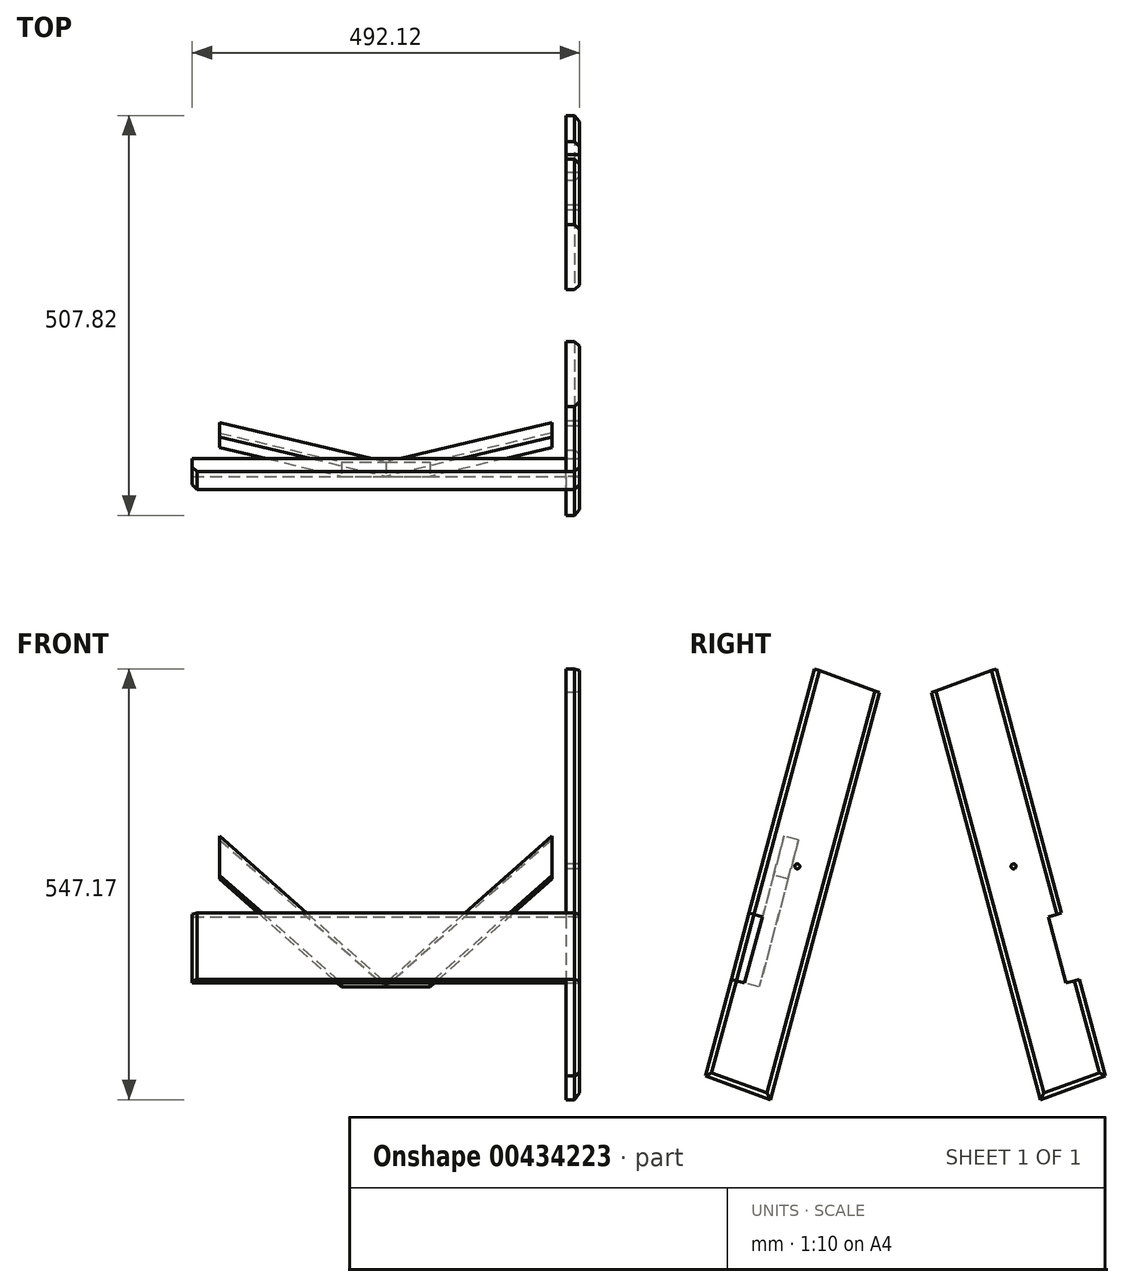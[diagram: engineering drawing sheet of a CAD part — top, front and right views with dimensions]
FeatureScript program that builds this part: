
annotation { "Feature Type Name" : "Feature", "Feature Type Description" : "" }
export const myFeature = defineFeature(function(context is Context, id is Id, definition is map)
    precondition{}
    {
        {
            var Q0;
            Q0=qCreatedBy(makeId("Right.planeOp"),FACE);
            var sketch = newSketch(context, id + "F0", { "sketchPlane" : qUnion([Q0])});
            skCircle(sketch, "E0", {"center": v(0, 0) * mm, "radius": 3.17 * mm, "construction": true});
            skCircle(sketch, "E1", {"center": v(0, 0) * mm, "radius": 43.66 * mm, "construction": true});
            skLineSegment(sketch, "E2", {"start": v(0, 0) * mm, "end": v(89.25, -32.49) * mm, "construction": true});
            skLineSegment(sketch, "E3", {"start": v(-42.17, 11.3) * mm, "end": v(42.17, -11.3) * mm, "construction": true});
            skLineSegment(sketch, "E4", {"start": v(22, 250.8) * mm, "end": v(-61.1, -59.39) * mm});
            skLineSegment(sketch, "E5", {"start": v(104.36, 220.82) * mm, "end": v(-34.22, -296.38) * mm});
            skLineSegment(sketch, "E6", {"start": v(22, 250.8) * mm, "end": v(104.36, 220.82) * mm});
            skLineSegment(sketch, "E7", {"start": v(-116.58, -266.4) * mm, "end": v(-34.22, -296.38) * mm});
            skCircle(sketch, "E8", {"center": v(0, 0) * mm, "radius": 3.13 * mm});
            skLineSegment(sketch, "E9", {"start": v(137.33, 282.03) * mm, "end": v(137.33, -341.7) * mm, "construction": true});
            skCircle(sketch, "E10.MirrorC", {"center": v(274.67, 0) * mm, "radius": 3.13 * mm});
            skCircle(sketch, "E11.MirrorC", {"center": v(274.67, 0) * mm, "radius": 3.17 * mm, "construction": true});
            skCircle(sketch, "E12.MirrorC", {"center": v(274.67, 0) * mm, "radius": 43.66 * mm, "construction": true});
            skLineSegment(sketch, "E13.MirrorCS", {"start": v(274.67, 0) * mm, "end": v(185.41, -32.49) * mm, "construction": true});
            skLineSegment(sketch, "E14.MirrorCS", {"start": v(316.83, 11.3) * mm, "end": v(232.5, -11.3) * mm, "construction": true});
            skLineSegment(sketch, "E15.MirrorCS", {"start": v(170.3, 220.82) * mm, "end": v(308.88, -296.38) * mm});
            skLineSegment(sketch, "E16.MirrorCS", {"start": v(252.66, 250.8) * mm, "end": v(170.3, 220.82) * mm});
            skLineSegment(sketch, "E17.MirrorCS", {"start": v(391.24, -266.4) * mm, "end": v(308.88, -296.38) * mm});
            skLineSegment(sketch, "E18", {"start": v(-61.1, -59.39) * mm, "end": v(-44.24, -63.9) * mm});
            skLineSegment(sketch, "E19", {"start": v(-44.24, -63.9) * mm, "end": v(-66.84, -148.25) * mm});
            skLineSegment(sketch, "E20", {"start": v(-66.84, -148.25) * mm, "end": v(-83.7, -143.73) * mm});
            skLineSegment(sketch, "E21.trimOffspring", {"start": v(-83.7, -143.73) * mm, "end": v(-116.58, -266.4) * mm});
            skLineSegment(sketch, "E22.MirrorCS", {"start": v(318.9, -63.9) * mm, "end": v(341.5, -148.25) * mm});
            skLineSegment(sketch, "E23.MirrorCS", {"start": v(335.77, -59.39) * mm, "end": v(318.9, -63.9) * mm});
            skLineSegment(sketch, "E24.MirrorCS", {"start": v(341.5, -148.25) * mm, "end": v(358.37, -143.73) * mm});
            skLineSegment(sketch, "E25.MirrorCS", {"start": v(252.66, 250.8) * mm, "end": v(335.77, -59.39) * mm});
            skLineSegment(sketch, "E26.MirrorCS", {"start": v(358.37, -143.73) * mm, "end": v(391.24, -266.4) * mm});
            skSolve(sketch);
        }
        {
            var Q0;
            Q0 = qSketchRegion(id + "F0", true);
            var Q1;
            Q1=makeQuery(id+"F0.imprint","IMPRINT",FACE,{"disambiguationData":[TD([[makeQuery(id+"F0.imprint","IMPRINT",EDGE,{"derivedFrom":sQuery(id+"F0.wireOp",EDGE,"E4")}),1.0]])]});
            extrude(context, id + "F1", {"entities" : qUnion([Q0, Q1]), "depth" : 17.46 * mm});
        }
        {
            var Q0;
            Q0=makeQuery(id+"F1.opExtrude","CAP_FACE",FACE,{"disambiguationData":[OSD([sQuery(id+"F0.wireOp",EDGE,"E4"),sQuery(id+"F0.wireOp",EDGE,"E5"),sQuery(id+"F0.wireOp",EDGE,"E6"),sQuery(id+"F0.wireOp",EDGE,"E7"),sQuery(id+"F0.wireOp",EDGE,"E8"),sQuery(id+"F0.wireOp",EDGE,"E18"),sQuery(id+"F0.wireOp",EDGE,"E19"),sQuery(id+"F0.wireOp",EDGE,"E20"),sQuery(id+"F0.wireOp",EDGE,"E21.trimOffspring")])],"isStart":false});
            var sketch = newSketch(context, id + "F2", { "sketchPlane" : qUnion([Q0])});
            skLineSegment(sketch, "E27", {"start": v(-44.24, -63.9) * mm, "end": v(-66.84, -148.25) * mm});
            skLineSegment(sketch, "E28", {"start": v(-66.84, -148.25) * mm, "end": v(-83.7, -143.73) * mm});
            skLineSegment(sketch, "E29", {"start": v(-83.7, -143.73) * mm, "end": v(-61.1, -59.39) * mm});
            skLineSegment(sketch, "E30", {"start": v(-61.1, -59.39) * mm, "end": v(-46.15, -63.4) * mm});
            skSolve(sketch);
        }
        {
            var Q0;
            Q0 = qSketchRegion(id + "F2", true);
            var Q1;
            {var subQ1=sQuery(id+"F2.wireOp",EDGE,"E27");Q1=makeQuery(id+"F2.imprint","IMPRINT",FACE,{"disambiguationData":[TD([[makeQuery(id+"F2.imprint","IMPRINT",EDGE,{"derivedFrom":subQ1}),-1.0]])]});}
            extrude(context, id + "F3", {"entities" : qUnion([Q0, Q1]), "depth" : -492.12 * mm});
        }
        {
            var Q0;
            Q0=makeQuery(id+"F3.opExtrude","CAP_EDGE",EDGE,{"disambiguationData":[OSD([sQuery(id+"F2.wireOp",EDGE,"E29")])],"isStart":true});
            var Q1;
            Q1=makeQuery(id+"F1.opExtrude","CAP_EDGE",EDGE,{"disambiguationData":[OSD([sQuery(id+"F0.wireOp",EDGE,"E4")])],"isStart":false});
            var Q2;
            Q2=makeQuery(id+"F1.opExtrude","CAP_EDGE",EDGE,{"disambiguationData":[OSD([sQuery(id+"F0.wireOp",EDGE,"E5")])],"isStart":false});
            var Q3;
            Q3=makeQuery(id+"F1.opExtrude","CAP_EDGE",EDGE,{"disambiguationData":[OSD([sQuery(id+"F0.wireOp",EDGE,"E21.trimOffspring")])],"isStart":false});
            var Q4;
            Q4=makeQuery(id+"F1.opExtrude","CAP_EDGE",EDGE,{"disambiguationData":[OSD([sQuery(id+"F0.wireOp",EDGE,"E7")])],"isStart":false});
            var Q5;
            Q5=makeQuery(id+"F1.opExtrude","CAP_EDGE",EDGE,{"disambiguationData":[OSD([sQuery(id+"F0.wireOp",EDGE,"E15.MirrorCS")])],"isStart":false});
            var Q6;
            Q6=makeQuery(id+"F1.opExtrude","CAP_EDGE",EDGE,{"disambiguationData":[OSD([sQuery(id+"F0.wireOp",EDGE,"E25.MirrorCS")])],"isStart":false});
            var Q7;
            Q7=makeQuery(id+"F1.opExtrude","CAP_EDGE",EDGE,{"disambiguationData":[OSD([sQuery(id+"F0.wireOp",EDGE,"E26.MirrorCS")])],"isStart":false});
            var Q8;
            Q8=makeQuery(id+"F1.opExtrude","CAP_EDGE",EDGE,{"disambiguationData":[OSD([sQuery(id+"F0.wireOp",EDGE,"E17.MirrorCS")])],"isStart":false});
            var Q9;
            Q9=makeQuery(id+"F3.opExtrude","CAP_EDGE",EDGE,{"disambiguationData":[OSD([sQuery(id+"F2.wireOp",EDGE,"E29")])],"isStart":false});
            chamfer(context, id + "F4", {"entities" : qUnion([Q0, Q1, Q2, Q3, Q4, Q5, Q6, Q7, Q8, Q9]), "width" : 6.35 * mm, "tangentPropagation" : true});
        }
        {
            var Q0;
            Q0=makeQuery(id+"F3.opExtrude","SWEPT_FACE",FACE,{"disambiguationData":[OSD([sQuery(id+"F2.wireOp",EDGE,"E27")])]});
            var sketch = newSketch(context, id + "F5", { "sketchPlane" : qUnion([Q0])});
            skLineSegment(sketch, "E31.MirrorCS", {"start": v(17.46, -18.7) * mm, "end": v(172.2, -160.5) * mm});
            skLineSegment(sketch, "E32.MirrorCS", {"start": v(172.2, -160.5) * mm, "end": v(228.6, -160.5) * mm});
            skLineSegment(sketch, "E33", {"start": v(17.46, -18.7) * mm, "end": v(17.46, -18.7) * mm});
            skLineSegment(sketch, "E34", {"start": v(17.46, 32.98) * mm, "end": v(228.6, -160.5) * mm});
            skLineSegment(sketch, "E35.bottom", {"start": v(17.46, 32.98) * mm, "end": v(439.74, 32.98) * mm, "construction": true});
            skLineSegment(sketch, "E35.right", {"start": v(439.74, 32.98) * mm, "end": v(439.74, -160.5) * mm, "construction": true});
            skLineSegment(sketch, "E36.bottom", {"start": v(439.74, 32.98) * mm, "end": v(474.66, 32.98) * mm, "construction": true});
            skLineSegment(sketch, "E36.top", {"start": v(439.74, -160.5) * mm, "end": v(474.66, -160.5) * mm, "construction": true});
            skLineSegment(sketch, "E36.right", {"start": v(474.66, 32.98) * mm, "end": v(474.66, -160.5) * mm, "construction": true});
            skLineSegment(sketch, "E37.bottom", {"start": v(17.46, 32.98) * mm, "end": v(-17.46, 32.98) * mm, "construction": true});
            skLineSegment(sketch, "E37.top", {"start": v(17.46, -160.5) * mm, "end": v(-17.46, -160.5) * mm, "construction": true});
            skLineSegment(sketch, "E37.right", {"start": v(-17.46, 32.98) * mm, "end": v(-17.46, -160.5) * mm, "construction": true});
            skLineSegment(sketch, "E38", {"start": v(17.46, -160.5) * mm, "end": v(172.2, -160.5) * mm, "construction": true});
            skLineSegment(sketch, "E39", {"start": v(228.6, 32.98) * mm, "end": v(228.6, -160.5) * mm, "construction": true});
            skLineSegment(sketch, "E40", {"start": v(228.6, -160.5) * mm, "end": v(439.74, -160.5) * mm, "construction": true});
            skLineSegment(sketch, "E41", {"start": v(17.46, -18.7) * mm, "end": v(17.46, 32.98) * mm});
            skLineSegment(sketch, "E42", {"start": v(17.46, -18.7) * mm, "end": v(17.46, -160.5) * mm, "construction": true});
            skLineSegment(sketch, "E43.MirrorCS", {"start": v(439.74, 32.98) * mm, "end": v(228.6, -160.5) * mm});
            skLineSegment(sketch, "E44.MirrorCS", {"start": v(439.74, -18.7) * mm, "end": v(439.74, 32.98) * mm});
            skLineSegment(sketch, "E45.MirrorCS", {"start": v(439.74, -18.7) * mm, "end": v(285, -160.5) * mm});
            skLineSegment(sketch, "E46.MirrorCS", {"start": v(285, -160.5) * mm, "end": v(228.6, -160.5) * mm});
            skSolve(sketch);
        }
        {
            var Q0;
            Q0 = qSketchRegion(id + "F5", true);
            extrude(context, id + "F6", {"entities" : qUnion([Q0]), "depth" : 19.05 * mm});
        }
    });
